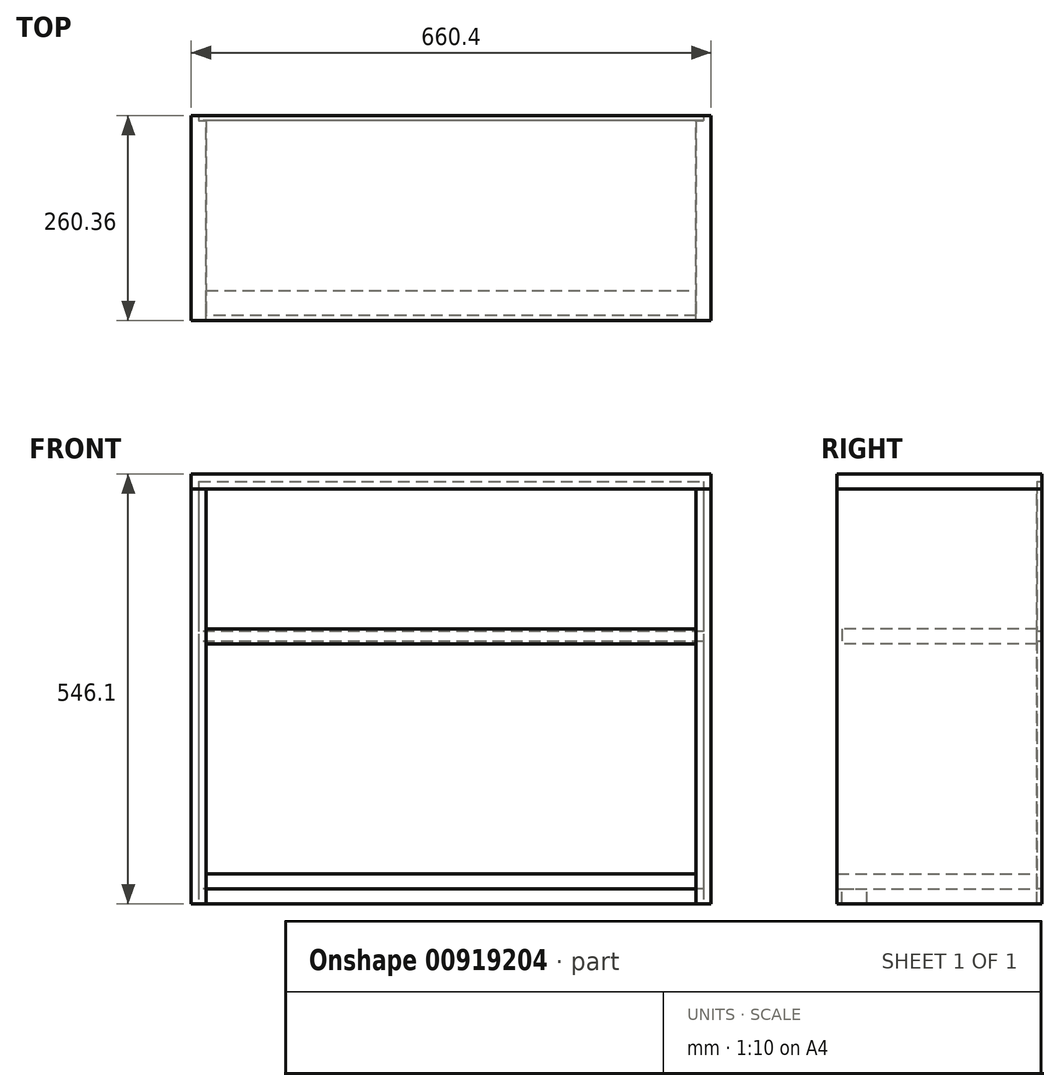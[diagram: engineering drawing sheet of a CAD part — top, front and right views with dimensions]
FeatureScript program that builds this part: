
annotation { "Feature Type Name" : "Feature", "Feature Type Description" : "" }
export const myFeature = defineFeature(function(context is Context, id is Id, definition is map)
    precondition{}
    {
        {
            var Q0;
            Q0=qCreatedBy(makeId("Top.planeOp"),FACE);
            var sketch = newSketch(context, id + "F0", { "sketchPlane" : qUnion([Q0])});
            skLineSegment(sketch, "E0.bottom", {"start": v(330.2, 130.17) * mm, "end": v(-330.2, 130.17) * mm});
            skLineSegment(sketch, "E0.top", {"start": v(330.2, -130.18) * mm, "end": v(-330.2, -130.18) * mm});
            skLineSegment(sketch, "E0.left", {"start": v(330.2, 130.17) * mm, "end": v(330.2, -130.18) * mm});
            skLineSegment(sketch, "E0.right", {"start": v(-330.2, 130.17) * mm, "end": v(-330.2, -130.18) * mm});
            skPoint(sketch, "E0.middle", {"position": v(0, 0) * mm});
            skSolve(sketch);
        }
        {
            var Q0;
            Q0 = qSketchRegion(id + "F0", true);
            extrude(context, id + "F1", {"entities" : qUnion([Q0]), "oppositeDirection" : true, "depth" : 19.05 * mm, "offsetDistance" : 25.4 * mm});
        }
        {
            var Q0;
            Q0=makeQuery(id+"F1.opExtrude","CAP_FACE",FACE,{"disambiguationData":[OSD([sQuery(id+"F0.wireOp",EDGE,"E0.bottom"),sQuery(id+"F0.wireOp",EDGE,"E0.top"),sQuery(id+"F0.wireOp",EDGE,"E0.left"),sQuery(id+"F0.wireOp",EDGE,"E0.right")])],"isStart":false});
            var sketch = newSketch(context, id + "F2", { "sketchPlane" : qUnion([Q0])});
            skLineSegment(sketch, "E1.bottom", {"start": v(-330.2, 130.18) * mm, "end": v(-311.15, 130.18) * mm});
            skLineSegment(sketch, "E1.top", {"start": v(-330.2, -130.17) * mm, "end": v(-311.15, -130.17) * mm});
            skLineSegment(sketch, "E1.left", {"start": v(-330.2, 130.18) * mm, "end": v(-330.2, -130.17) * mm});
            skLineSegment(sketch, "E1.right", {"start": v(-311.15, 130.18) * mm, "end": v(-311.15, -130.17) * mm});
            skLineSegment(sketch, "E2.bottom", {"start": v(330.2, 130.18) * mm, "end": v(311.15, 130.18) * mm});
            skLineSegment(sketch, "E2.top", {"start": v(330.2, -130.17) * mm, "end": v(311.15, -130.17) * mm});
            skLineSegment(sketch, "E2.left", {"start": v(330.2, 130.18) * mm, "end": v(330.2, -130.17) * mm});
            skLineSegment(sketch, "E2.right", {"start": v(311.15, 130.18) * mm, "end": v(311.15, -130.17) * mm});
            skSolve(sketch);
        }
        {
            var Q0;
            Q0 = qSketchRegion(id + "F2", true);
            extrude(context, id + "F3", {"entities" : qUnion([Q0]), "depth" : 527.05 * mm, "offsetDistance" : 25.4 * mm});
        }
        {
            var Q0;
            Q0=makeQuery(id+"F3.opExtrude","SWEPT_FACE",FACE,{"disambiguationData":[OSD([sQuery(id+"F2.wireOp",EDGE,"E1.right")])]});
            var sketch = newSketch(context, id + "F4", { "sketchPlane" : qUnion([Q0])});
            skLineSegment(sketch, "E3.bottom", {"start": v(-130.18, -508) * mm, "end": v(130.17, -508) * mm});
            skLineSegment(sketch, "E3.top", {"start": v(-130.18, -527.05) * mm, "end": v(130.17, -527.05) * mm});
            skLineSegment(sketch, "E3.left", {"start": v(-130.18, -508) * mm, "end": v(-130.18, -527.05) * mm});
            skLineSegment(sketch, "E3.right", {"start": v(130.17, -508) * mm, "end": v(130.17, -527.05) * mm});
            skSolve(sketch);
        }
        {
            var Q0;
            Q0 = qSketchRegion(id + "F4", true);
            extrude(context, id + "F5", {"entities" : qUnion([Q0]), "endBound" : BoundingType.UP_TO_NEXT, "depth" : 25.4 * mm, "offsetDistance" : 25.4 * mm});
        }
        {
            var Q0;
            Q0=makeQuery(id+"F5.opExtrude","SWEPT_FACE",FACE,{"disambiguationData":[OSD([sQuery(id+"F4.wireOp",EDGE,"E3.top")])]});
            var sketch = newSketch(context, id + "F6", { "sketchPlane" : qUnion([Q0])});
            skLineSegment(sketch, "E4.bottom", {"start": v(-311.15, 123.83) * mm, "end": v(311.15, 123.83) * mm});
            skLineSegment(sketch, "E4.top", {"start": v(-311.15, 92.08) * mm, "end": v(311.15, 92.08) * mm});
            skLineSegment(sketch, "E4.left", {"start": v(-311.15, 123.83) * mm, "end": v(-311.15, 92.08) * mm});
            skLineSegment(sketch, "E4.right", {"start": v(311.15, 123.83) * mm, "end": v(311.15, 92.08) * mm});
            skSolve(sketch);
        }
        {
            var Q0;
            Q0 = qSketchRegion(id + "F6", true);
            var Q1;
            Q1=makeQuery(id+"F3.opExtrude","CAP_FACE",FACE,{"disambiguationData":[OSD([sQuery(id+"F2.wireOp",EDGE,"E1.bottom"),sQuery(id+"F2.wireOp",EDGE,"E1.top"),sQuery(id+"F2.wireOp",EDGE,"E1.left"),sQuery(id+"F2.wireOp",EDGE,"E1.right")])],"isStart":false});
            extrude(context, id + "F7", {"entities" : qUnion([Q0]), "endBound" : BoundingType.UP_TO_SURFACE, "depth" : 25.4 * mm, "endBoundEntityFace" : qUnion([Q1]), "offsetDistance" : 25.4 * mm});
        }
        {
            var Q0;
            Q0=makeQuery(id+"F1.opExtrude","SWEPT_FACE",FACE,{"disambiguationData":[OSD([sQuery(id+"F0.wireOp",EDGE,"E0.bottom")])]});
            var sketch = newSketch(context, id + "F8", { "sketchPlane" : qUnion([Q0])});
            skLineSegment(sketch, "E5.bottom", {"start": v(320.67, -9.53) * mm, "end": v(-320.68, -9.53) * mm});
            skLineSegment(sketch, "E5.top", {"start": v(320.68, -546.1) * mm, "end": v(-320.68, -546.1) * mm});
            skLineSegment(sketch, "E5.left", {"start": v(320.67, -9.53) * mm, "end": v(320.68, -546.1) * mm});
            skLineSegment(sketch, "E5.right", {"start": v(-320.68, -9.53) * mm, "end": v(-320.68, -546.1) * mm});
            skPoint(sketch, "E6", {"position": v(330.2, -9.53) * mm});
            skSolve(sketch);
        }
        {
            var Q0;
            Q0 = qSketchRegion(id + "F8", true);
            extrude(context, id + "F9", {"entities" : qUnion([Q0]), "operationType" : NewBodyOperationType.REMOVE, "oppositeDirection" : true, "depth" : 6.35 * mm, "offsetDistance" : 25.4 * mm});
        }
        {
            var Q0;
            Q0=makeQuery(id+"F3.opExtrude","SWEPT_FACE",FACE,{"disambiguationData":[OSD([sQuery(id+"F2.wireOp",EDGE,"E1.right")])]});
            var sketch = newSketch(context, id + "F10", { "sketchPlane" : qUnion([Q0])});
            skLineSegment(sketch, "E7.bottom", {"start": v(123.82, -196.85) * mm, "end": v(-123.83, -196.85) * mm});
            skLineSegment(sketch, "E7.top", {"start": v(123.82, -215.9) * mm, "end": v(-123.83, -215.9) * mm});
            skLineSegment(sketch, "E7.left", {"start": v(123.82, -196.85) * mm, "end": v(123.82, -215.9) * mm});
            skLineSegment(sketch, "E7.right", {"start": v(-123.83, -196.85) * mm, "end": v(-123.83, -215.9) * mm});
            skSolve(sketch);
        }
        {
            var Q0;
            Q0=makeQuery(id+"F10.imprint","IMPRINT",FACE,{"disambiguationData":[TD([[makeQuery(id+"F10.imprint","IMPRINT",EDGE,{"derivedFrom":sQuery(id+"F10.wireOp",EDGE,"E7.bottom")}),1.0]])]});
            extrude(context, id + "F11", {"entities" : qUnion([Q0]), "endBound" : BoundingType.UP_TO_NEXT, "depth" : 25.4 * mm, "offsetDistance" : 25.4 * mm});
        }
        {
            var Q0;
            {var subQ0=sQuery(id+"F8.wireOp",EDGE,"E5.bottom");var subQ1=sQuery(id+"F8.wireOp",EDGE,"E5.right");var subQ2=sQuery(id+"F8.wireOp",EDGE,"E5.left");Q0=makeQuery(id+"F9.boolean.opBoolean","COPY",FACE,{"disambiguationData":[TD([makeQuery(id+"F9.opExtrude","SWEPT_FACE",FACE,{"disambiguationData":[OSD([subQ0])]})])],"derivedFrom":makeQuery(id+"F9.opExtrude","CAP_FACE",FACE,{"disambiguationData":[OSD([subQ0,sQuery(id+"F8.wireOp",EDGE,"E5.top"),subQ2,subQ1])],"isStart":false})});}
            var sketch = newSketch(context, id + "F12", { "sketchPlane" : qUnion([Q0])});
            skLineSegment(sketch, "E8.bottom", {"start": v(-320.68, -9.53) * mm, "end": v(320.67, -9.53) * mm});
            skLineSegment(sketch, "E8.top", {"start": v(-320.68, -200.02) * mm, "end": v(320.67, -200.02) * mm});
            skLineSegment(sketch, "E8.left", {"start": v(-320.68, -9.53) * mm, "end": v(-320.68, -200.02) * mm});
            skLineSegment(sketch, "E8.right", {"start": v(320.67, -9.53) * mm, "end": v(320.67, -200.02) * mm});
            skLineSegment(sketch, "E9.bottom", {"start": v(-320.68, -212.72) * mm, "end": v(320.67, -212.72) * mm});
            skLineSegment(sketch, "E9.top", {"start": v(-320.68, -527.05) * mm, "end": v(320.67, -527.05) * mm});
            skLineSegment(sketch, "E9.left", {"start": v(-320.68, -212.72) * mm, "end": v(-320.68, -527.05) * mm});
            skLineSegment(sketch, "E9.right", {"start": v(320.67, -212.72) * mm, "end": v(320.67, -527.05) * mm});
            skSolve(sketch);
        }
        {
            var Q0;
            {var subQ0=sQuery(id+"F12.wireOp",EDGE,"E8.top");Q0=makeQuery(id+"F12.imprint","IMPRINT",FACE,{"disambiguationData":[TD([[makeQuery(id+"F12.imprint","IMPRINT",EDGE,{"derivedFrom":subQ0}),1.0]])]});}
            var Q1;
            Q1=makeQuery(id+"F12.imprint","IMPRINT",FACE,{"disambiguationData":[TD([[makeQuery(id+"F12.imprint","IMPRINT",EDGE,{"derivedFrom":sQuery(id+"F12.wireOp",EDGE,"E9.bottom")}),-1.0]])]});
            var Q2;
            {var subQ0=sQuery(id+"F12.wireOp",EDGE,"E8.bottom");Q2=makeQuery(id+"F12.imprint","IMPRINT",FACE,{"disambiguationData":[TD([[makeQuery(id+"F12.imprint","IMPRINT",EDGE,{"derivedFrom":subQ0}),1.0]])]});}
            var Q3;
            Q3=makeQuery(id+"F3.opExtrude","SWEPT_FACE",FACE,{"disambiguationData":[OSD([sQuery(id+"F2.wireOp",EDGE,"E2.top")])]});
            extrude(context, id + "F13", {"entities" : qUnion([Q0, Q1, Q2]), "endBound" : BoundingType.UP_TO_SURFACE, "depth" : 25.4 * mm, "endBoundEntityFace" : qUnion([Q3]), "offsetDistance" : 25.4 * mm});
        }
    });
